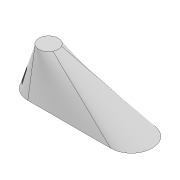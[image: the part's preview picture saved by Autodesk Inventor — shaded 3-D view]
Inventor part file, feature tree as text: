
AUTODESK INVENTOR PART (.ipt)
format: ipt  version: 2022 (Build 260153000, 153)  size: 439,296 bytes
history: native  units: mm
features: sketch x8, extrude x5, plane x2, loft x2, fillet x2, shell x1, projected_geometry x1
ambient origin geometry x8: Origin, YZ Plane, XZ Plane, XY Plane, X Axis, Y Axis, Z Axis, Center Point
bodies: Solid1 (feature_tree)
feature tree (21):
  sketch  "Sketch1"  dims[d0=14.0mm d3=-28.0mm d4=30.0mm]
  plane  "Work Plane3"
  loft  "Loft1"
  shell  "Shell1"  Thickness=30.0mm
  extrude  "Extrusion11"  TaperAngle=0.0deg  [1 undecoded]
  sketch  "Sketch9"  dims[d8=0.0mm d9=90.0deg d10=3.5mm]
  extrude  "Extrusion6"  Depth=3.5mm
  extrude  "Extrusion7"  Depth=10.0mm TaperAngle=0.0deg
  sketch  "Sketch10"  dims[d53=5.0mm d54=10.0mm d55=0.0mm]
  plane  "Work Plane4"
  loft  "Loft2"
  extrude  "Extrusion8"  Depth=9.0mm
  fillet  "Fillet1"  [1 undecoded]
  fillet  "Fillet2"  [1 undecoded]
  extrude  "Extrusion10"  Depth=30.0mm TaperAngle=0.0deg
  sketch  "Sketch3"  dims[d5=60.0mm d6=0.0mm d7=90.0deg]
  projected_geometry  "Projected Loop2"
  sketch  "Sketch11"  dims[d56=5.0mm d57=0.0mm d58=10.2mm]
  sketch  "Sketch12"  dims[d59=25.0mm d60=9.0mm d61=0.0mm d62=90.0deg d63=0.0mm d64=90.0deg]
  sketch  "Sketch15"  dims[d65=5.0mm d66=30.0mm d67=0.0mm]
  sketch  "Sketch16"  dims[d68=2.0mm d69=2.0mm d72=40.0mm d74=6.0mm d75=10.0mm d77=10.0mm d79=5.0mm d80=0.0mm d81=4.0mm d82=8.0mm d83=1.5mm d84=8.0mm d85=100.0mm d86=0.0mm]
note: 3 required parameter values undecoded (feature->parameter linkage not recoverable at this tier; creation-order binding heuristic only, values carry confidence <= 0.55)
